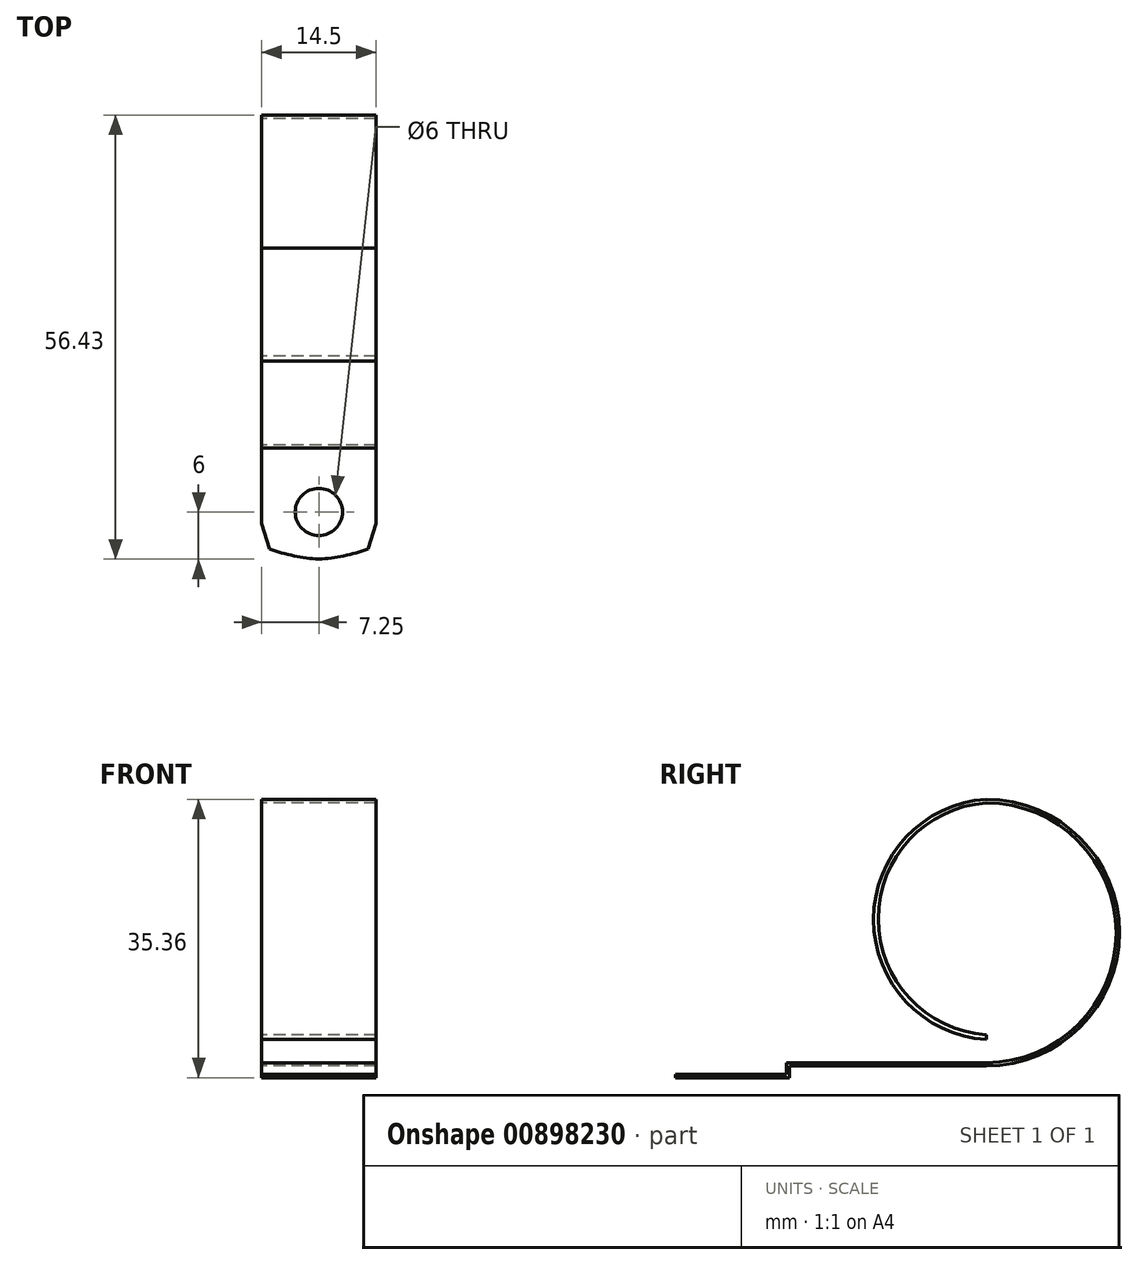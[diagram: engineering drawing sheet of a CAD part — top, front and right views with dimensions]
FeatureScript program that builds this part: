
annotation { "Feature Type Name" : "Feature", "Feature Type Description" : "" }
export const myFeature = defineFeature(function(context is Context, id is Id, definition is map)
    precondition{}
    {
        {
            var Q0;
            Q0=qCreatedBy(makeId("Right.planeOp"),FACE);
            var sketch = newSketch(context, id + "F0", { "sketchPlane" : qUnion([Q0])});
            skLineSegment(sketch, "E0", {"start": v(14.1, 0) * mm, "end": v(14.1, -0.4) * mm});
            skLineSegment(sketch, "E1", {"start": v(14.5, -0.4) * mm, "end": v(39.5, -0.4) * mm});
            skLineSegment(sketch, "E2", {"start": v(14.5, 0) * mm, "end": v(39.5, 0) * mm});
            skArc(sketch, "E3", {"start": v(39.5, 0) * mm, "mid": v(56, 16.5) * mm, "end": v(39.5, 33) * mm});
            skArc(sketch, "E4", {"start": v(39.5, -0.4) * mm, "mid": v(56.43, 16.53) * mm, "end": v(39.5, 33.46) * mm});
            skArc(sketch, "E5", {"start": v(39.5, 33) * mm, "mid": v(25.78, 18.27) * mm, "end": v(39.5, 3.54) * mm});
            skArc(sketch, "E6", {"start": v(39.5, 33.46) * mm, "mid": v(25.18, 18.2) * mm, "end": v(39.5, 2.94) * mm});
            skLineSegment(sketch, "E7", {"start": v(39.5, 2.94) * mm, "end": v(39.5, 3.54) * mm});
            skLineSegment(sketch, "E8", {"start": v(14.1, -0.4) * mm, "end": v(14.1, -1.5) * mm});
            skLineSegment(sketch, "E9", {"start": v(14.1, -1.5) * mm, "end": v(0, -1.5) * mm});
            skLineSegment(sketch, "E10", {"start": v(0, -1.5) * mm, "end": v(0, -1.9) * mm});
            skLineSegment(sketch, "E11", {"start": v(0, -1.9) * mm, "end": v(14.5, -1.9) * mm});
            skLineSegment(sketch, "E12", {"start": v(14.5, -1.9) * mm, "end": v(14.5, -0.4) * mm});
            skLineSegment(sketch, "E13", {"start": v(14.1, 0) * mm, "end": v(14.5, 0) * mm});
            skSolve(sketch);
        }
        {
            var Q0;
            Q0=qSketchRegion(id+"F0",true);
            extrude(context, id + "F1", {"entities" : qUnion([Q0]), "endBound" : BoundingType.SYMMETRIC, "depth" : 14.5 * mm});
        }
        {
            var Q0;
            Q0=makeQuery(id+"F1.opExtrude","SWEPT_FACE",FACE,{"disambiguationData":[OSD([sQuery(id+"F0.wireOp",EDGE,"E9")])]});
            var sketch = newSketch(context, id + "F2", { "sketchPlane" : qUnion([Q0])});
            skArc(sketch, "E14", {"start": v(-6.23, 1.27) * mm, "mid": v(-3.16, 0.43) * mm, "end": v(0, 0) * mm});
            skLineSegment(sketch, "E15", {"start": v(-6.23, 1.27) * mm, "end": v(-7.25, 4.56) * mm});
            skLineSegment(sketch, "E16", {"start": v(0, 0) * mm, "end": v(-7.25, 0) * mm});
            skLineSegment(sketch, "E17", {"start": v(-7.25, 0) * mm, "end": v(-7.25, 4.56) * mm});
            skCircle(sketch, "E18", {"center": v(0, 6) * mm, "radius": 3 * mm});
            skArc(sketch, "E19.MirrorCS", {"start": v(6.23, 1.27) * mm, "mid": v(3.16, 0.43) * mm, "end": v(0, 0) * mm});
            skLineSegment(sketch, "E20.MirrorCS", {"start": v(6.23, 1.27) * mm, "end": v(7.25, 4.56) * mm});
            skLineSegment(sketch, "E21.MirrorCS", {"start": v(7.25, 0) * mm, "end": v(7.25, 4.56) * mm});
            skLineSegment(sketch, "E22.MirrorCS", {"start": v(0, 0) * mm, "end": v(7.25, 0) * mm});
            skSolve(sketch);
        }
        {
            var Q0;
            Q0=qSketchRegion(id+"F2",true);
            extrude(context, id + "F3", {"entities" : qUnion([Q0]), "operationType" : NewBodyOperationType.REMOVE, "oppositeDirection" : true, "depth" : 25 * mm});
        }
    });
